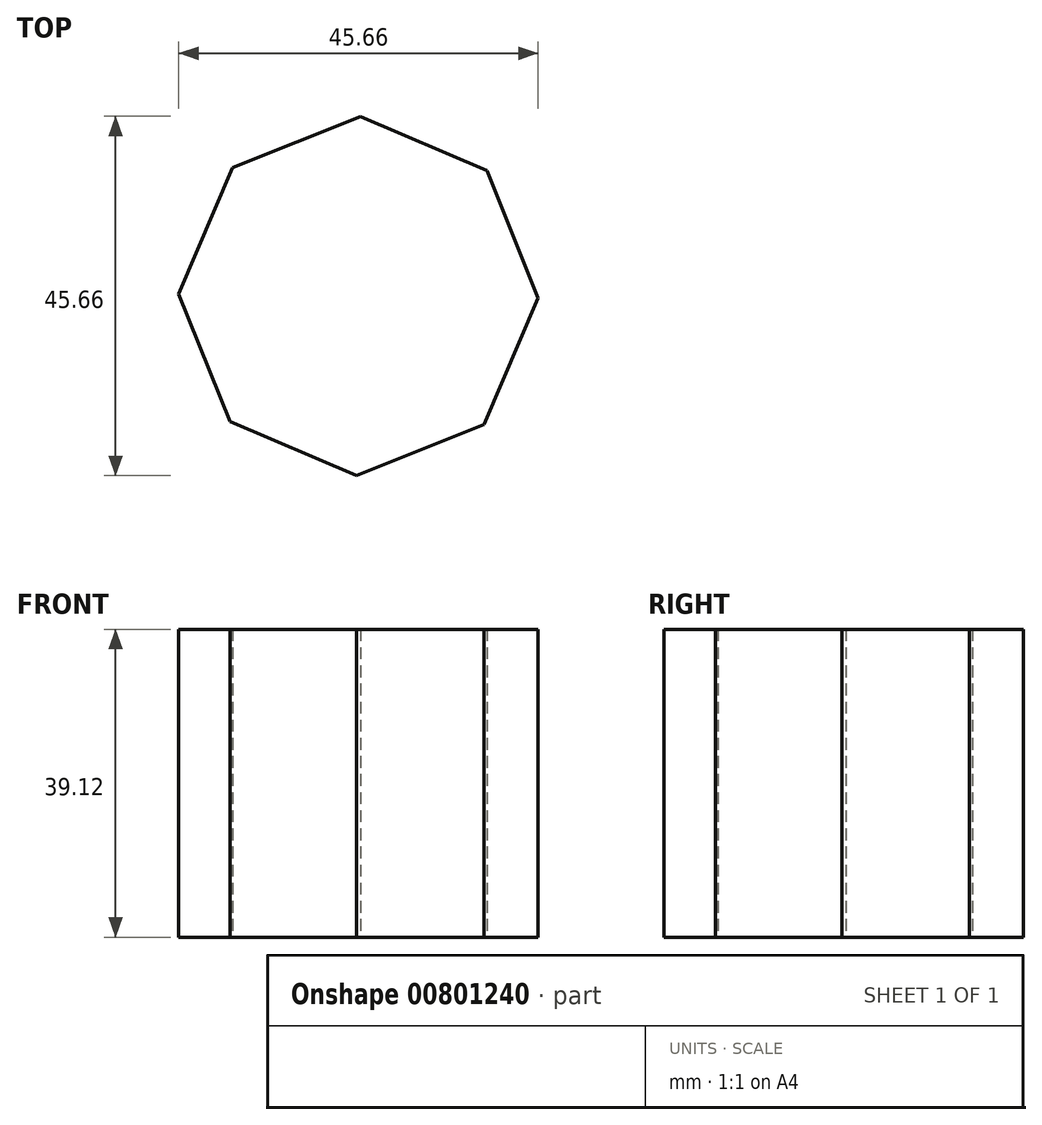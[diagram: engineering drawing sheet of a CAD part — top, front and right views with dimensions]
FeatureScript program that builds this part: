
annotation { "Feature Type Name" : "Feature", "Feature Type Description" : "" }
export const myFeature = defineFeature(function(context is Context, id is Id, definition is map)
    precondition{}
    {
        {
            var Q0;
            Q0=qCreatedBy(makeId("Top.planeOp"),FACE);
            var sketch = newSketch(context, id + "F0", { "sketchPlane" : qUnion([Q0])});
            skCircle(sketch, "E0", {"center": v(0, 0) * mm, "radius": 45.73 * mm});
            skCircle(sketch, "E1", {"center": v(40.65, 25.47) * mm, "radius": 7.02 * mm});
            skSolve(sketch);
        }
        {
            var Q0;
            Q0=sQuery(id+"F0.wireOp",EDGE,"E1");
            extrude(context, id + "F1", {"bodyType" : ToolBodyType.SURFACE, "surfaceEntities" : qUnion([Q0]), "depth" : 45.72 * mm, "offsetDistance" : 25.4 * mm});
        }
        {
            var Q0;
            Q0=qCreatedBy(makeId("Top.planeOp"),FACE);
            var sketch = newSketch(context, id + "F2", { "sketchPlane" : qUnion([Q0])});
            skCircle(sketch, "E2.cCircle", {"center": v(0, 0) * mm, "radius": 21.09 * mm, "construction": true});
            skLineSegment(sketch, "E2.0", {"start": v(16.32, 15.96) * mm, "end": v(22.83, -0.25) * mm});
            skLineSegment(sketch, "E2.1", {"start": v(22.83, -0.25) * mm, "end": v(15.96, -16.32) * mm});
            skLineSegment(sketch, "E2.2", {"start": v(15.96, -16.32) * mm, "end": v(-0.25, -22.83) * mm});
            skLineSegment(sketch, "E2.3", {"start": v(-0.25, -22.83) * mm, "end": v(-16.32, -15.96) * mm});
            skLineSegment(sketch, "E2.4", {"start": v(-16.32, -15.96) * mm, "end": v(-22.83, 0.25) * mm});
            skLineSegment(sketch, "E2.5", {"start": v(-22.83, 0.25) * mm, "end": v(-15.96, 16.32) * mm});
            skLineSegment(sketch, "E2.6", {"start": v(-15.96, 16.32) * mm, "end": v(0.25, 22.83) * mm});
            skLineSegment(sketch, "E2.7", {"start": v(0.25, 22.83) * mm, "end": v(16.32, 15.96) * mm});
            skPoint(sketch, "E2.0.midPoint", {"position": v(19.57, 7.86) * mm});
            skSolve(sketch);
        }
        {
            var Q0;
            Q0 = qSketchRegion(id + "F2", true);
            extrude(context, id + "F3", {"entities" : qUnion([Q0]), "depth" : 39.12 * mm, "offsetDistance" : 25.4 * mm});
        }
    });
